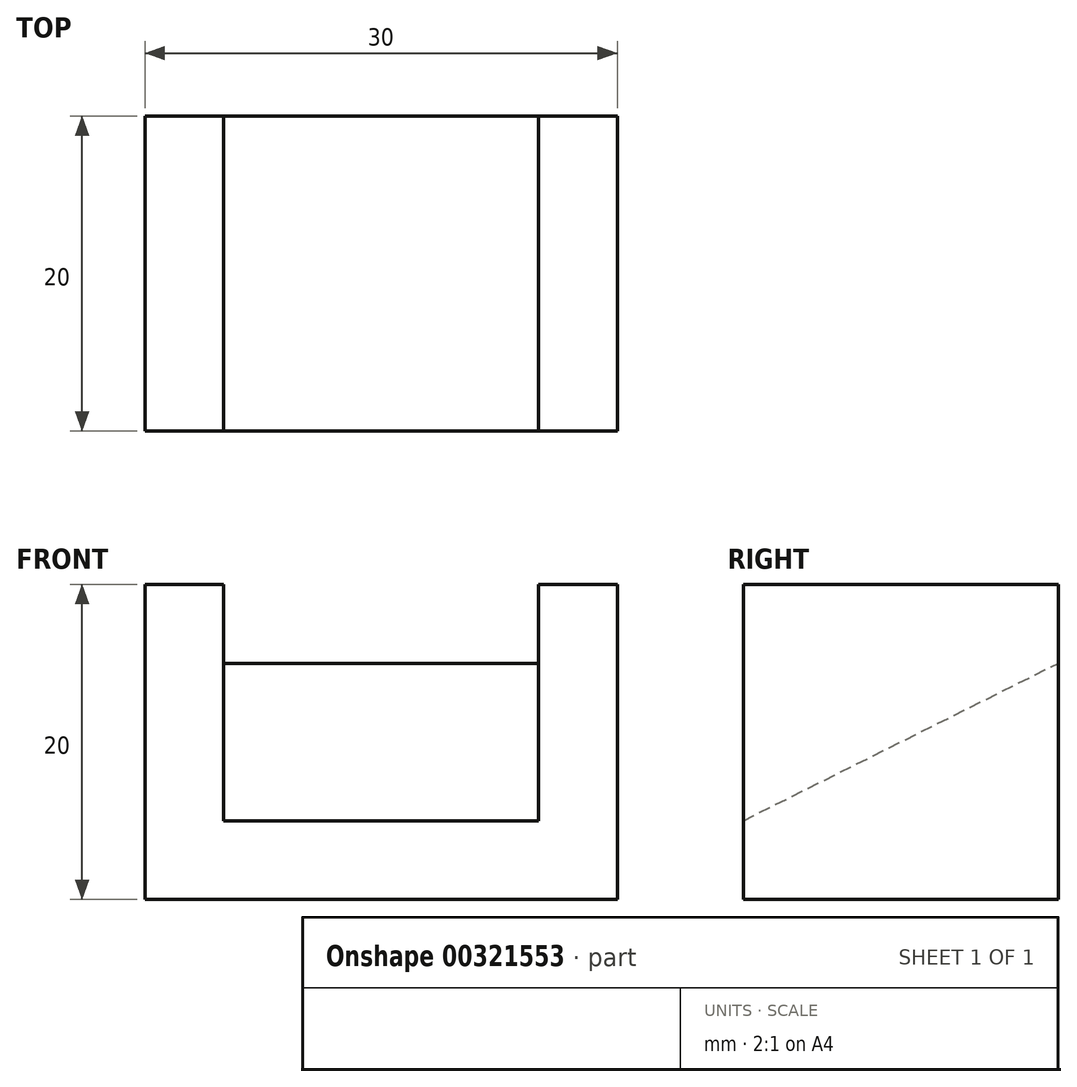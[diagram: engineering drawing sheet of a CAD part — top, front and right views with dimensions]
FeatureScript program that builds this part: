
annotation { "Feature Type Name" : "Feature", "Feature Type Description" : "" }
export const myFeature = defineFeature(function(context is Context, id is Id, definition is map)
    precondition{}
    {
        {
            var Q0;
            Q0=qCreatedBy(makeId("Right.planeOp"),FACE);
            var sketch = newSketch(context, id + "F0", { "sketchPlane" : qUnion([Q0])});
            skPoint(sketch, "E0.0", {"position": v(0, 0) * mm});
            skLineSegment(sketch, "E1.bottom", {"start": v(0, 0) * mm, "end": v(20, 0) * mm});
            skLineSegment(sketch, "E1.top", {"start": v(0, 20) * mm, "end": v(20, 20) * mm});
            skLineSegment(sketch, "E1.left", {"start": v(0, 0) * mm, "end": v(0, 20) * mm});
            skLineSegment(sketch, "E1.right", {"start": v(20, 0) * mm, "end": v(20, 20) * mm});
            skLineSegment(sketch, "E2", {"start": v(0, 20) * mm, "end": v(0, 5) * mm});
            skLineSegment(sketch, "E3", {"start": v(0, 5) * mm, "end": v(20, 15) * mm});
            skLineSegment(sketch, "E4", {"start": v(20, 15) * mm, "end": v(20, 20) * mm});
            skSolve(sketch);
        }
        {
            var Q0;
            Q0=makeQuery(id+"F0.imprint","IMPRINT",FACE,{"disambiguationData":[TD([[makeQuery(id+"F0.imprint","IMPRINT",EDGE,{"derivedFrom":sQuery(id+"F0.wireOp",EDGE,"E1.bottom")}),1.0]])]});
            extrude(context, id + "F1", {"entities" : qUnion([Q0]), "depth" : 30 * mm});
        }
        {
            var Q0;
            Q0=makeQuery(id+"F0.imprint","IMPRINT",FACE,{"disambiguationData":[TD([[makeQuery(id+"F0.imprint","IMPRINT",EDGE,{"derivedFrom":sQuery(id+"F0.wireOp",EDGE,"E1.top")}),-1.0]])]});
            extrude(context, id + "F2", {"entities" : qUnion([Q0]), "operationType" : NewBodyOperationType.ADD, "depth" : 5 * mm});
        }
        {
            var Q0;
            Q0=makeQuery(id+"F1.opExtrude","CAP_FACE",FACE,{"disambiguationData":[OSD([sQuery(id+"F0.wireOp",EDGE,"E1.bottom"),sQuery(id+"F0.wireOp",EDGE,"E1.left"),sQuery(id+"F0.wireOp",EDGE,"E1.right"),sQuery(id+"F0.wireOp",EDGE,"E3")])],"isStart":false});
            var sketch = newSketch(context, id + "F3", { "sketchPlane" : qUnion([Q0])});
            skLineSegment(sketch, "E5", {"start": v(0, 5) * mm, "end": v(20, 15) * mm});
            skLineSegment(sketch, "E6", {"start": v(20, 15) * mm, "end": v(20, 20) * mm});
            skLineSegment(sketch, "E7", {"start": v(20, 20) * mm, "end": v(0, 20) * mm});
            skLineSegment(sketch, "E8", {"start": v(0, 20) * mm, "end": v(0, 5) * mm});
            skSolve(sketch);
        }
        {
            var Q0;
            Q0=makeQuery(id+"F3.imprint","IMPRINT",FACE,{"disambiguationData":[TD([[makeQuery(id+"F3.imprint","IMPRINT",EDGE,{"derivedFrom":sQuery(id+"F3.wireOp",EDGE,"E5")}),1.0]])]});
            extrude(context, id + "F4", {"entities" : qUnion([Q0]), "operationType" : NewBodyOperationType.ADD, "oppositeDirection" : true, "depth" : 5 * mm});
        }
    });
